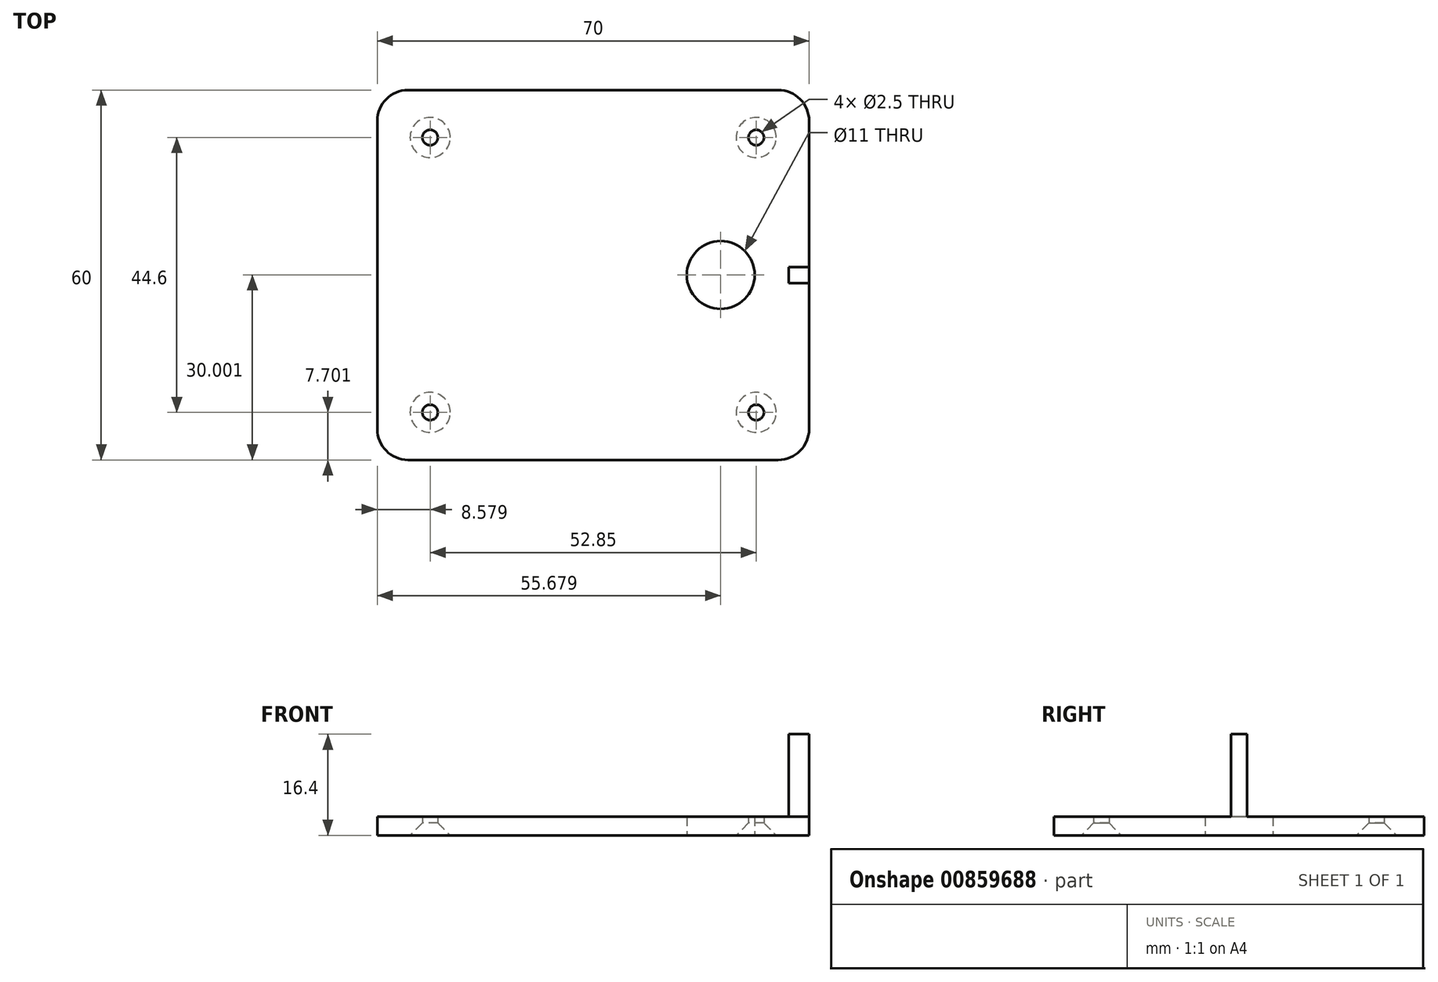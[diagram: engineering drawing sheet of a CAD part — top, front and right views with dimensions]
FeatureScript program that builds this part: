
annotation { "Feature Type Name" : "Feature", "Feature Type Description" : "" }
export const myFeature = defineFeature(function(context is Context, id is Id, definition is map)
    precondition{}
    {
        {
            var Q0;
            Q0=qCreatedBy(makeId("Top.planeOp"),FACE);
            var sketch = newSketch(context, id + "F0", { "sketchPlane" : qUnion([Q0])});
            skLineSegment(sketch, "E0.0.0", {"start": v(17.07, 9.28) * mm, "end": v(13.75, 9.28) * mm});
            skLineSegment(sketch, "E0.0.1", {"start": v(13.75, 9.28) * mm, "end": v(13.75, -4.02) * mm});
            skLineSegment(sketch, "E0.0.2", {"start": v(13.75, -4.02) * mm, "end": v(3.25, -4.02) * mm});
            skLineSegment(sketch, "E0.0.3", {"start": v(3.25, -4.02) * mm, "end": v(3.25, -5.95) * mm});
            skArc(sketch, "E0.0.4", {"start": v(3.25, -5.95) * mm, "mid": v(-0.85, -10.05) * mm, "end": v(-4.95, -5.95) * mm});
            skLineSegment(sketch, "E0.0.5", {"start": v(-4.95, -5.95) * mm, "end": v(-4.95, -4.02) * mm});
            skLineSegment(sketch, "E0.0.6", {"start": v(-4.95, -4.02) * mm, "end": v(-30.9, -4.02) * mm});
            skLineSegment(sketch, "E0.0.7", {"start": v(-30.9, -4.02) * mm, "end": v(-30.9, -5.95) * mm});
            skArc(sketch, "E0.0.8", {"start": v(-30.9, -5.95) * mm, "mid": v(-35, -10.05) * mm, "end": v(-39.1, -5.95) * mm});
            skLineSegment(sketch, "E0.0.9", {"start": v(-39.1, -5.95) * mm, "end": v(-39.1, -4.02) * mm});
            skLineSegment(sketch, "E0.0.10", {"start": v(-39.1, -4.02) * mm, "end": v(-49.6, -4.02) * mm});
            skLineSegment(sketch, "E0.0.11", {"start": v(-49.6, -4.02) * mm, "end": v(-49.6, 25.18) * mm});
            skLineSegment(sketch, "E0.0.12", {"start": v(-49.6, 25.18) * mm, "end": v(-39.1, 25.18) * mm});
            skLineSegment(sketch, "E0.0.13", {"start": v(-39.1, 25.18) * mm, "end": v(-39.1, 27.1) * mm});
            skArc(sketch, "E0.0.14", {"start": v(-39.1, 27.1) * mm, "mid": v(-35, 31.2) * mm, "end": v(-30.9, 27.1) * mm});
            skLineSegment(sketch, "E0.0.15", {"start": v(-30.9, 27.1) * mm, "end": v(-30.9, 25.18) * mm});
            skLineSegment(sketch, "E0.0.16", {"start": v(-30.9, 25.18) * mm, "end": v(-4.95, 25.18) * mm});
            skLineSegment(sketch, "E0.0.17", {"start": v(-4.95, 25.18) * mm, "end": v(-4.95, 27.1) * mm});
            skArc(sketch, "E0.0.18", {"start": v(-4.95, 27.1) * mm, "mid": v(-0.85, 31.2) * mm, "end": v(3.25, 27.1) * mm});
            skLineSegment(sketch, "E0.0.19", {"start": v(3.25, 27.1) * mm, "end": v(3.25, 25.18) * mm});
            skLineSegment(sketch, "E0.0.20", {"start": v(3.25, 25.18) * mm, "end": v(13.75, 25.18) * mm});
            skLineSegment(sketch, "E0.0.21", {"start": v(13.75, 25.18) * mm, "end": v(13.75, 11.88) * mm});
            skLineSegment(sketch, "E0.0.22", {"start": v(13.75, 11.88) * mm, "end": v(17.07, 11.88) * mm});
            skLineSegment(sketch, "E0.0.23", {"start": v(17.07, 11.88) * mm, "end": v(17.07, 40.58) * mm});
            skLineSegment(sketch, "E0.0.24", {"start": v(17.07, 40.58) * mm, "end": v(-52.93, 40.58) * mm});
            skLineSegment(sketch, "E0.0.25", {"start": v(-52.93, 40.58) * mm, "end": v(-52.93, -19.42) * mm});
            skLineSegment(sketch, "E0.0.26", {"start": v(-52.93, -19.42) * mm, "end": v(17.07, -19.42) * mm});
            skLineSegment(sketch, "E0.0.27", {"start": v(17.07, -19.42) * mm, "end": v(17.07, 9.28) * mm});
            skCircle(sketch, "E1.0", {"center": v(-44.35, 32.88) * mm, "radius": 1.25 * mm});
            skCircle(sketch, "E2.0", {"center": v(8.5, 32.88) * mm, "radius": 1.25 * mm});
            skCircle(sketch, "E3.0", {"center": v(8.5, -11.72) * mm, "radius": 1.25 * mm});
            skCircle(sketch, "E4.0", {"center": v(-44.35, -11.72) * mm, "radius": 1.25 * mm});
            skLineSegment(sketch, "E5", {"start": v(13.75, 11.88) * mm, "end": v(13.75, 9.28) * mm});
            skLineSegment(sketch, "E6", {"start": v(17.07, 9.28) * mm, "end": v(17.07, 11.88) * mm});
            skCircle(sketch, "E7", {"center": v(2.75, 10.58) * mm, "radius": 5.5 * mm});
            skPoint(sketch, "E7.centerSnap0", {"position": v(13.75, 10.58) * mm});
            skSolve(sketch);
        }
        {
            var Q0;
            Q0=makeQuery(id+"F0.imprint","IMPRINT",FACE,{"disambiguationData":[TD([[makeQuery(id+"F0.imprint","IMPRINT",EDGE,{"derivedFrom":sQuery(id+"F0.wireOp",EDGE,"E0.0.0")}),1.0]])]});
            var Q1;
            Q1=makeQuery(id+"F0.imprint","IMPRINT",FACE,{"disambiguationData":[TD([[makeQuery(id+"F0.imprint","IMPRINT",EDGE,{"derivedFrom":sQuery(id+"F0.wireOp",EDGE,"E0.0.1")}),-1.0]])]});
            extrude(context, id + "F1", {"entities" : qUnion([Q0, Q1]), "depth" : 3 * mm, "offsetDistance" : 25 * mm});
        }
        {
            var Q0;
            Q0=makeQuery(id+"F1.opExtrude","CAP_FACE",FACE,{"disambiguationData":[OSD([sQuery(id+"F0.wireOp",EDGE,"E0.0.0"),sQuery(id+"F0.wireOp",EDGE,"E0.0.22"),sQuery(id+"F0.wireOp",EDGE,"E0.0.23"),sQuery(id+"F0.wireOp",EDGE,"E0.0.24"),sQuery(id+"F0.wireOp",EDGE,"E0.0.25"),sQuery(id+"F0.wireOp",EDGE,"E0.0.26"),sQuery(id+"F0.wireOp",EDGE,"E0.0.27"),sQuery(id+"F0.wireOp",EDGE,"E1.0"),sQuery(id+"F0.wireOp",EDGE,"E2.0"),sQuery(id+"F0.wireOp",EDGE,"E3.0"),sQuery(id+"F0.wireOp",EDGE,"E4.0"),sQuery(id+"F0.wireOp",EDGE,"E5"),sQuery(id+"F0.wireOp",EDGE,"E7")])],"isStart":true});
            var sketch = newSketch(context, id + "F2", { "sketchPlane" : qUnion([Q0])});
            skLineSegment(sketch, "E8.bottom", {"start": v(13.75, -11.88) * mm, "end": v(17.07, -11.88) * mm});
            skLineSegment(sketch, "E8.top", {"start": v(13.75, -9.28) * mm, "end": v(17.07, -9.28) * mm});
            skLineSegment(sketch, "E8.left", {"start": v(13.75, -11.88) * mm, "end": v(13.75, -9.28) * mm});
            skLineSegment(sketch, "E8.right", {"start": v(17.07, -11.88) * mm, "end": v(17.07, -9.28) * mm});
            skSolve(sketch);
        }
        {
            var Q0;
            Q0=makeQuery(id+"F2.imprint","IMPRINT",FACE,{"disambiguationData":[TD([[makeQuery(id+"F2.imprint","IMPRINT",EDGE,{"derivedFrom":sQuery(id+"F2.wireOp",EDGE,"E8.bottom")}),1.0]])]});
            extrude(context, id + "F3", {"entities" : qUnion([Q0]), "operationType" : NewBodyOperationType.ADD, "oppositeDirection" : true, "depth" : 16.4 * mm, "offsetDistance" : 25 * mm});
        }
        {
            var Q0;
            Q0=makeQuery(id+"F1.opExtrude","CAP_EDGE",EDGE,{"disambiguationData":[OSD([sQuery(id+"F0.wireOp",EDGE,"E4.0")])],"isStart":true});
            var Q1;
            Q1=makeQuery(id+"F1.opExtrude","CAP_EDGE",EDGE,{"disambiguationData":[OSD([sQuery(id+"F0.wireOp",EDGE,"E1.0")])],"isStart":true});
            var Q2;
            Q2=makeQuery(id+"F1.opExtrude","CAP_EDGE",EDGE,{"disambiguationData":[OSD([sQuery(id+"F0.wireOp",EDGE,"E2.0")])],"isStart":true});
            var Q3;
            Q3=makeQuery(id+"F1.opExtrude","CAP_EDGE",EDGE,{"disambiguationData":[OSD([sQuery(id+"F0.wireOp",EDGE,"E3.0")])],"isStart":true});
            chamfer(context, id + "F4", {"entities" : qUnion([Q0, Q1, Q2, Q3]), "width" : 2 * mm, "tangentPropagation" : true});
        }
        {
            var Q0;
            Q0=makeQuery(id+"F1.opExtrude","SWEPT_EDGE",EDGE,{"disambiguationData":[OSD([sQuery(id+"F0.wireOp",EDGE,"E0.0.25"),sQuery(id+"F0.wireOp",EDGE,"E0.0.26")])]});
            var Q1;
            Q1=makeQuery(id+"F1.opExtrude","SWEPT_EDGE",EDGE,{"disambiguationData":[OSD([sQuery(id+"F0.wireOp",EDGE,"E0.0.26"),sQuery(id+"F0.wireOp",EDGE,"E0.0.27")])]});
            var Q2;
            Q2=makeQuery(id+"F1.opExtrude","SWEPT_EDGE",EDGE,{"disambiguationData":[OSD([sQuery(id+"F0.wireOp",EDGE,"E0.0.23"),sQuery(id+"F0.wireOp",EDGE,"E0.0.24")])]});
            var Q3;
            Q3=makeQuery(id+"F1.opExtrude","SWEPT_EDGE",EDGE,{"disambiguationData":[OSD([sQuery(id+"F0.wireOp",EDGE,"E0.0.24"),sQuery(id+"F0.wireOp",EDGE,"E0.0.25")])]});
            fillet(context, id + "F5", {"entities" : qUnion([Q0, Q1, Q2, Q3]), "radius" : 5 * mm, "tangentPropagation" : true, "allowEdgeOverflow" : false});
        }
    });
